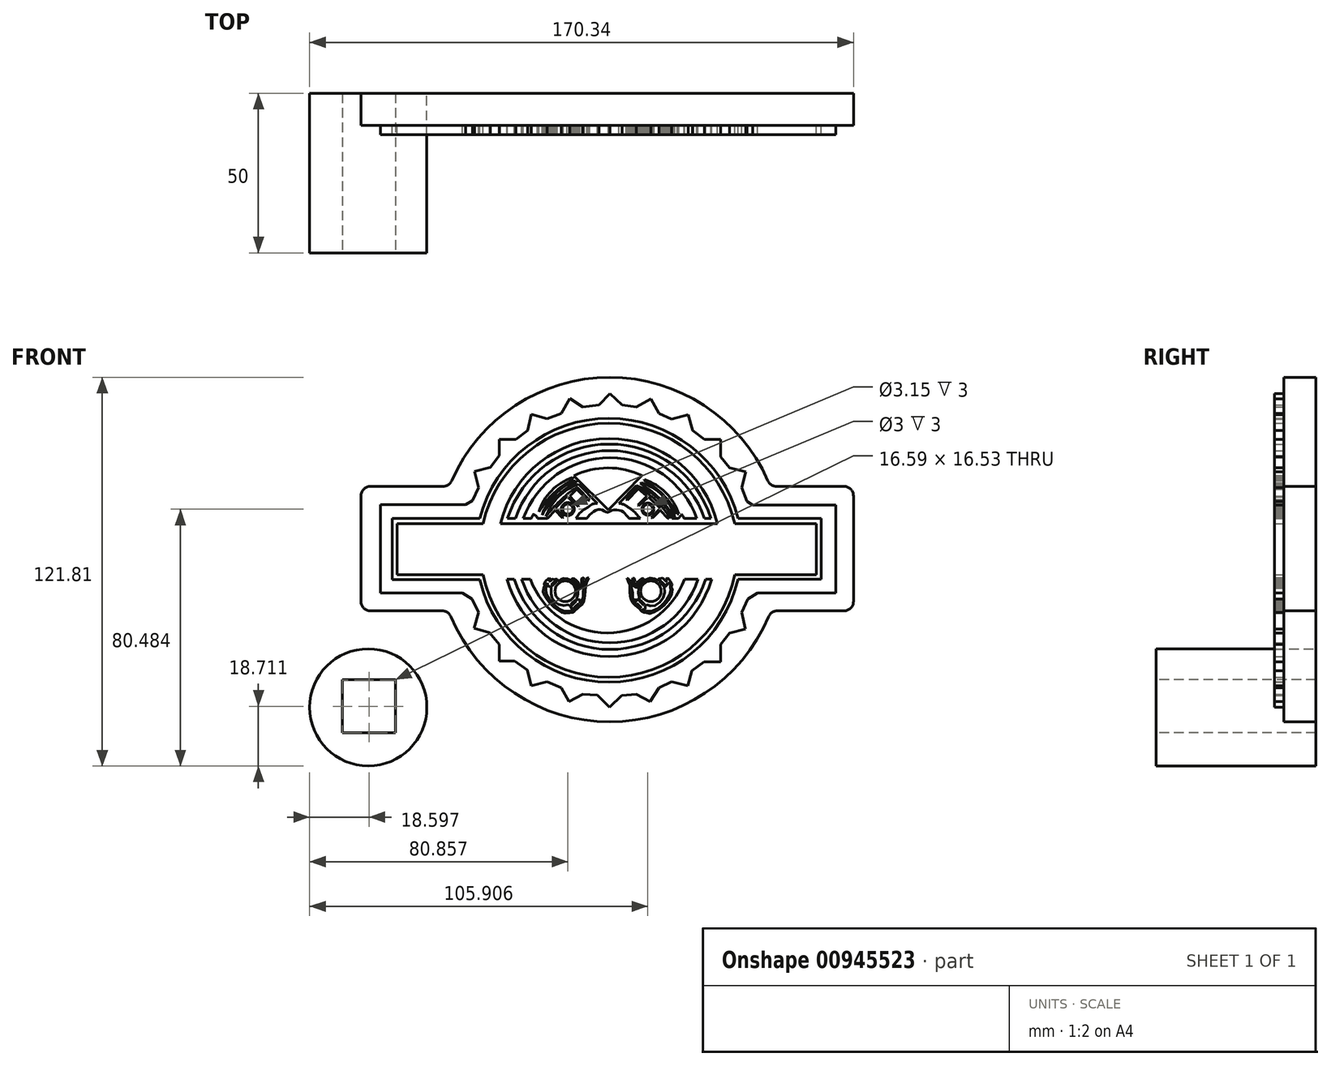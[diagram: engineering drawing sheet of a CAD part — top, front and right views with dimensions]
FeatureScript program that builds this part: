
annotation { "Feature Type Name" : "Feature", "Feature Type Description" : "" }
export const myFeature = defineFeature(function(context is Context, id is Id, definition is map)
    precondition{}
    {
        {
            var Q0;
            Q0=qCreatedBy(makeId("Front.planeOp"),FACE);
            var sketch = newSketch(context, id + "F0", { "sketchPlane" : qUnion([Q0])});
            skArc(sketch, "E0", {"start": v(25.18, 30.24) * mm, "mid": v(75.64, -4.55) * mm, "end": v(126.1, 30.24) * mm});
            skLineSegment(sketch, "E1.0", {"start": v(-2.31, 69.26) * mm, "end": v(25.4, 69.26) * mm});
            skLineSegment(sketch, "E1.1", {"start": v(-2.31, 69.26) * mm, "end": v(-2.31, 30.24) * mm});
            skLineSegment(sketch, "E1.2", {"start": v(-2.31, 30.24) * mm, "end": v(25.18, 30.24) * mm});
            skLineSegment(sketch, "E1.3", {"start": v(151.98, 69.26) * mm, "end": v(151.98, 30.24) * mm});
            skLineSegment(sketch, "E2.trimOffspring", {"start": v(125.88, 69.26) * mm, "end": v(151.98, 69.26) * mm});
            skArc(sketch, "E3.trimOffspring", {"start": v(125.88, 69.26) * mm, "mid": v(75.64, 103.45) * mm, "end": v(25.4, 69.26) * mm});
            skLineSegment(sketch, "E4.trimOffspring", {"start": v(126.1, 30.24) * mm, "end": v(151.98, 30.24) * mm});
            skSolve(sketch);
        }
        {
            var Q0;
            Q0=qCreatedBy(makeId("Front.planeOp"),FACE);
            var sketch = newSketch(context, id + "F1", { "sketchPlane" : qUnion([Q0])});
            skLineSegment(sketch, "E5", {"start": v(30.5, 63.54) * mm, "end": v(3.78, 63.54) * mm});
            skLineSegment(sketch, "E6", {"start": v(3.78, 63.54) * mm, "end": v(3.78, 35.86) * mm});
            skLineSegment(sketch, "E7", {"start": v(3.78, 35.86) * mm, "end": v(29.45, 35.86) * mm});
            skLineSegment(sketch, "E8", {"start": v(29.45, 35.86) * mm, "end": v(32.5, 33.94) * mm});
            skLineSegment(sketch, "E9", {"start": v(32.5, 33.94) * mm, "end": v(34.52, 29.75) * mm});
            skLineSegment(sketch, "E10", {"start": v(34.52, 29.75) * mm, "end": v(33.12, 24.77) * mm});
            skLineSegment(sketch, "E11", {"start": v(33.12, 24.77) * mm, "end": v(37.98, 23.4) * mm});
            skLineSegment(sketch, "E12", {"start": v(37.98, 23.4) * mm, "end": v(40.98, 19.7) * mm});
            skLineSegment(sketch, "E13", {"start": v(40.98, 19.7) * mm, "end": v(40.98, 14.56) * mm});
            skLineSegment(sketch, "E14", {"start": v(40.98, 14.56) * mm, "end": v(45.87, 14.56) * mm});
            skLineSegment(sketch, "E15", {"start": v(45.87, 14.56) * mm, "end": v(49.8, 11.67) * mm});
            skLineSegment(sketch, "E16", {"start": v(49.8, 11.67) * mm, "end": v(51.1, 6.79) * mm});
            skLineSegment(sketch, "E17", {"start": v(51.1, 6.79) * mm, "end": v(55.98, 8.09) * mm});
            skLineSegment(sketch, "E18", {"start": v(55.98, 8.09) * mm, "end": v(60.45, 6.09) * mm});
            skLineSegment(sketch, "E19", {"start": v(60.45, 6.09) * mm, "end": v(62.83, 1.76) * mm});
            skLineSegment(sketch, "E20", {"start": v(62.83, 1.76) * mm, "end": v(67.2, 4.17) * mm});
            skLineSegment(sketch, "E21", {"start": v(67.2, 4.17) * mm, "end": v(71.82, 3.86) * mm});
            skLineSegment(sketch, "E22", {"start": v(71.82, 3.86) * mm, "end": v(75.57, 0) * mm});
            skLineSegment(sketch, "E23", {"start": v(75.57, 0) * mm, "end": v(79.4, 3.73) * mm});
            skLineSegment(sketch, "E24", {"start": v(79.4, 3.73) * mm, "end": v(84.01, 4.17) * mm});
            skLineSegment(sketch, "E25", {"start": v(84.01, 4.17) * mm, "end": v(88.3, 1.76) * mm});
            skLineSegment(sketch, "E26", {"start": v(88.3, 1.76) * mm, "end": v(91.06, 6.09) * mm});
            skLineSegment(sketch, "E27", {"start": v(91.06, 6.09) * mm, "end": v(95.06, 8.09) * mm});
            skLineSegment(sketch, "E28", {"start": v(95.06, 8.09) * mm, "end": v(100.1, 6.76) * mm});
            skLineSegment(sketch, "E29", {"start": v(100.1, 6.76) * mm, "end": v(101.35, 11.5) * mm});
            skLineSegment(sketch, "E30", {"start": v(101.35, 11.5) * mm, "end": v(105.12, 14.32) * mm});
            skLineSegment(sketch, "E31", {"start": v(105.12, 14.32) * mm, "end": v(110.37, 14.32) * mm});
            skLineSegment(sketch, "E32", {"start": v(110.37, 14.32) * mm, "end": v(110.37, 19.7) * mm});
            skLineSegment(sketch, "E33", {"start": v(110.37, 19.7) * mm, "end": v(113.14, 23.25) * mm});
            skLineSegment(sketch, "E34", {"start": v(113.14, 23.25) * mm, "end": v(118.13, 24.58) * mm});
            skLineSegment(sketch, "E35", {"start": v(118.13, 24.58) * mm, "end": v(116.98, 29.75) * mm});
            skLineSegment(sketch, "E36", {"start": v(116.98, 29.75) * mm, "end": v(118.86, 33.93) * mm});
            skLineSegment(sketch, "E37", {"start": v(118.86, 33.93) * mm, "end": v(121.91, 35.86) * mm});
            skLineSegment(sketch, "E38", {"start": v(121.91, 35.86) * mm, "end": v(146.4, 35.86) * mm});
            skLineSegment(sketch, "E39", {"start": v(146.4, 35.86) * mm, "end": v(146.4, 63.36) * mm});
            skLineSegment(sketch, "E40", {"start": v(146.4, 63.36) * mm, "end": v(120.45, 63.36) * mm});
            skLineSegment(sketch, "E41", {"start": v(120.45, 63.36) * mm, "end": v(118.6, 64.53) * mm});
            skLineSegment(sketch, "E42", {"start": v(118.6, 64.53) * mm, "end": v(117.02, 68.85) * mm});
            skLineSegment(sketch, "E43", {"start": v(117.02, 68.85) * mm, "end": v(118.21, 73.83) * mm});
            skLineSegment(sketch, "E44", {"start": v(118.21, 73.83) * mm, "end": v(113.14, 75.04) * mm});
            skLineSegment(sketch, "E45", {"start": v(113.14, 75.04) * mm, "end": v(110.4, 78.55) * mm});
            skLineSegment(sketch, "E46", {"start": v(110.4, 78.55) * mm, "end": v(110.4, 83.96) * mm});
            skLineSegment(sketch, "E47", {"start": v(110.4, 83.96) * mm, "end": v(105.25, 83.96) * mm});
            skLineSegment(sketch, "E48", {"start": v(105.25, 83.96) * mm, "end": v(101.62, 86.75) * mm});
            skLineSegment(sketch, "E49", {"start": v(101.62, 86.75) * mm, "end": v(100.26, 91.8) * mm});
            skLineSegment(sketch, "E50", {"start": v(100.26, 91.8) * mm, "end": v(95, 90.39) * mm});
            skLineSegment(sketch, "E51", {"start": v(95, 90.39) * mm, "end": v(91.04, 92.16) * mm});
            skLineSegment(sketch, "E52", {"start": v(91.04, 92.16) * mm, "end": v(88.5, 96.65) * mm});
            skLineSegment(sketch, "E53", {"start": v(88.5, 96.65) * mm, "end": v(84.01, 94.11) * mm});
            skLineSegment(sketch, "E54", {"start": v(84.01, 94.11) * mm, "end": v(79.45, 94.74) * mm});
            skLineSegment(sketch, "E55", {"start": v(79.45, 94.74) * mm, "end": v(75.74, 98.35) * mm});
            skLineSegment(sketch, "E56", {"start": v(75.74, 98.35) * mm, "end": v(72.22, 94.74) * mm});
            skLineSegment(sketch, "E57", {"start": v(72.22, 94.74) * mm, "end": v(67.2, 94.19) * mm});
            skLineSegment(sketch, "E58", {"start": v(67.2, 94.19) * mm, "end": v(63.1, 96.84) * mm});
            skLineSegment(sketch, "E59", {"start": v(63.1, 96.84) * mm, "end": v(60.45, 92.16) * mm});
            skLineSegment(sketch, "E60", {"start": v(60.45, 92.16) * mm, "end": v(55.98, 90.42) * mm});
            skLineSegment(sketch, "E61", {"start": v(55.98, 90.42) * mm, "end": v(51.1, 91.9) * mm});
            skLineSegment(sketch, "E62", {"start": v(51.1, 91.9) * mm, "end": v(49.88, 86.75) * mm});
            skLineSegment(sketch, "E63", {"start": v(49.88, 86.75) * mm, "end": v(46.18, 83.96) * mm});
            skLineSegment(sketch, "E64", {"start": v(46.18, 83.96) * mm, "end": v(40.98, 83.96) * mm});
            skLineSegment(sketch, "E65", {"start": v(40.98, 83.96) * mm, "end": v(40.98, 78.87) * mm});
            skLineSegment(sketch, "E66", {"start": v(40.98, 78.87) * mm, "end": v(38.2, 75.25) * mm});
            skLineSegment(sketch, "E67", {"start": v(38.2, 75.25) * mm, "end": v(33.23, 73.92) * mm});
            skLineSegment(sketch, "E68", {"start": v(33.23, 73.92) * mm, "end": v(34.52, 68.85) * mm});
            skLineSegment(sketch, "E69", {"start": v(34.52, 68.85) * mm, "end": v(32.7, 64.8) * mm});
            skLineSegment(sketch, "E70", {"start": v(32.7, 64.8) * mm, "end": v(30.5, 63.54) * mm});
            skLineSegment(sketch, "E71", {"start": v(9.03, 41.6) * mm, "end": v(35.92, 41.6) * mm});
            skLineSegment(sketch, "E72", {"start": v(41.42, 41.6) * mm, "end": v(109.35, 41.6) * mm});
            skLineSegment(sketch, "E73", {"start": v(114.78, 41.6) * mm, "end": v(140.34, 41.6) * mm});
            skLineSegment(sketch, "E74", {"start": v(140.34, 41.6) * mm, "end": v(140.34, 57.63) * mm});
            skLineSegment(sketch, "E75", {"start": v(140.34, 57.63) * mm, "end": v(114.78, 57.63) * mm});
            skLineSegment(sketch, "E76", {"start": v(109.35, 57.63) * mm, "end": v(41.42, 57.63) * mm});
            skLineSegment(sketch, "E77", {"start": v(35.92, 57.63) * mm, "end": v(9.03, 57.63) * mm});
            skLineSegment(sketch, "E78", {"start": v(9.03, 57.63) * mm, "end": v(9.03, 41.6) * mm});
            skLineSegment(sketch, "E79", {"start": v(34.93, 40.01) * mm, "end": v(7.52, 40.01) * mm});
            skLineSegment(sketch, "E80", {"start": v(7.52, 40.01) * mm, "end": v(7.52, 59.18) * mm});
            skLineSegment(sketch, "E81", {"start": v(7.52, 59.18) * mm, "end": v(34.93, 59.18) * mm});
            skLineSegment(sketch, "E82", {"start": v(33.62, 37.96) * mm, "end": v(5.73, 37.96) * mm});
            skLineSegment(sketch, "E83", {"start": v(5.73, 37.96) * mm, "end": v(5.73, 61.27) * mm});
            skLineSegment(sketch, "E84", {"start": v(5.73, 61.27) * mm, "end": v(33.62, 61.27) * mm});
            skLineSegment(sketch, "E85", {"start": v(117.62, 37.9) * mm, "end": v(144.3, 37.9) * mm});
            skLineSegment(sketch, "E86", {"start": v(144.3, 37.9) * mm, "end": v(144.3, 61.3) * mm});
            skLineSegment(sketch, "E87", {"start": v(144.3, 61.3) * mm, "end": v(117.62, 61.3) * mm});
            skLineSegment(sketch, "E88", {"start": v(115.83, 40.18) * mm, "end": v(141.89, 40.18) * mm});
            skLineSegment(sketch, "E89", {"start": v(141.89, 40.18) * mm, "end": v(141.89, 59.2) * mm});
            skLineSegment(sketch, "E90", {"start": v(141.89, 59.2) * mm, "end": v(115.83, 59.2) * mm});
            skArc(sketch, "E91", {"start": v(117.62, 61.3) * mm, "mid": v(75.61, 92.75) * mm, "end": v(33.62, 61.27) * mm});
            skArc(sketch, "E92", {"start": v(33.62, 37.96) * mm, "mid": v(75.6, 5.72) * mm, "end": v(117.62, 37.9) * mm});
            skArc(sketch, "E93", {"start": v(115.83, 59.2) * mm, "mid": v(75.38, 90.6) * mm, "end": v(34.93, 59.18) * mm});
            skArc(sketch, "E94", {"start": v(114.78, 57.63) * mm, "mid": v(75.35, 89.03) * mm, "end": v(35.92, 57.63) * mm});
            skArc(sketch, "E95", {"start": v(34.93, 40.01) * mm, "mid": v(75.45, 7.9) * mm, "end": v(115.83, 40.18) * mm});
            skArc(sketch, "E96", {"start": v(35.92, 41.6) * mm, "mid": v(75.35, 9.41) * mm, "end": v(114.78, 41.6) * mm});
            skArc(sketch, "E97", {"start": v(109.35, 57.63) * mm, "mid": v(75.39, 84.29) * mm, "end": v(41.42, 57.63) * mm});
            skArc(sketch, "E98", {"start": v(41.42, 41.6) * mm, "mid": v(75.39, 14.36) * mm, "end": v(109.35, 41.6) * mm});
            skLineSegment(sketch, "E99", {"start": v(43.44, 40.2) * mm, "end": v(45.7, 40.2) * mm});
            skLineSegment(sketch, "E100", {"start": v(107.38, 59.2) * mm, "end": v(105.28, 59.2) * mm});
            skArc(sketch, "E101", {"start": v(43.44, 40.2) * mm, "mid": v(75.49, 15.92) * mm, "end": v(107.53, 40.2) * mm});
            skArc(sketch, "E102", {"start": v(45.7, 40.2) * mm, "mid": v(75.66, 18.15) * mm, "end": v(105.62, 40.2) * mm});
            skArc(sketch, "E103", {"start": v(48.04, 40.2) * mm, "mid": v(75.68, 20.21) * mm, "end": v(103.32, 40.2) * mm});
            skArc(sketch, "E104", {"start": v(50.75, 40.2) * mm, "mid": v(74.89, 23.3) * mm, "end": v(99.03, 40.2) * mm});
            skArc(sketch, "E105", {"start": v(107.38, 59.2) * mm, "mid": v(75.5, 82.51) * mm, "end": v(43.63, 59.2) * mm});
            skArc(sketch, "E106", {"start": v(105.28, 59.2) * mm, "mid": v(75.68, 80.48) * mm, "end": v(46.08, 59.2) * mm});
            skArc(sketch, "E107", {"start": v(102.92, 59.2) * mm, "mid": v(75.72, 78.24) * mm, "end": v(48.53, 59.2) * mm});
            skLineSegment(sketch, "E108.trimOffspring", {"start": v(46.08, 59.2) * mm, "end": v(43.63, 59.2) * mm});
            skLineSegment(sketch, "E109.trimOffspring", {"start": v(102.92, 59.2) * mm, "end": v(98.91, 59.2) * mm});
            skLineSegment(sketch, "E110.trimOffspring", {"start": v(105.62, 40.2) * mm, "end": v(107.53, 40.2) * mm});
            skLineSegment(sketch, "E111.trimOffspring", {"start": v(48.04, 40.2) * mm, "end": v(50.75, 40.2) * mm});
            skLineSegment(sketch, "E112.trimOffspring", {"start": v(99.03, 40.2) * mm, "end": v(103.32, 40.2) * mm});
            skCircle(sketch, "E113", {"center": v(61.71, 36.41) * mm, "radius": 3.23 * mm});
            skCircle(sketch, "E114", {"center": v(88.52, 36.41) * mm, "radius": 3.23 * mm});
            skFitSpline(sketch, "E115", {"points": [v(68.46, 59.2) * mm, v(69.7, 60.65) * mm, v(71.48, 61.83) * mm, v(73.15, 61.95) * mm, v(74.42, 61.27) * mm, v(75.13, 61.15) * mm, v(75.93, 61.58) * mm, v(77.56, 61.95) * mm, v(79.42, 61.49) * mm, v(80.68, 60.44) * mm, v(81.6, 59.2) * mm], "startDerivative": vector(10.07, 13.37) * mm, "endDerivative": vector(8.68, -12.6) * mm});
            skLineSegment(sketch, "E116.trimOffspring", {"start": v(68.46, 59.2) * mm, "end": v(64.99, 59.2) * mm});
            skLineSegment(sketch, "E117", {"start": v(85.75, 72.69) * mm, "end": v(75.16, 61.95) * mm});
            skLineSegment(sketch, "E118", {"start": v(75.16, 61.95) * mm, "end": v(64.39, 72.57) * mm});
            skArc(sketch, "E119", {"start": v(85.75, 72.69) * mm, "mid": v(75.05, 75.05) * mm, "end": v(64.39, 72.57) * mm});
            skFitSpline(sketch, "E120", {"points": [v(51.11, 59.2) * mm, v(51.37, 59.89) * mm, v(51.77, 60.51) * mm, v(51.88, 60.44) * mm, v(52.58, 60) * mm, v(52.99, 59.2) * mm], "startDerivative": vector(0.9, 2.92) * mm, "endDerivative": vector(1.1, -3.69) * mm});
            skFitSpline(sketch, "E121", {"points": [v(98.91, 59.2) * mm, v(98.65, 59.79) * mm, v(98.16, 60.47) * mm, v(98.07, 60.32) * mm, v(97.9, 60.15) * mm, v(97.17, 59.2) * mm], "startDerivative": vector(-0.86, 2.35) * mm, "endDerivative": vector(-2.85, -4.03) * mm});
            skLineSegment(sketch, "E122.trimOffspring", {"start": v(97.17, 59.2) * mm, "end": v(95.18, 59.2) * mm});
            skLineSegment(sketch, "E123.trimOffspring", {"start": v(51.11, 59.2) * mm, "end": v(48.53, 59.2) * mm});
            skFitSpline(sketch, "E124", {"points": [v(56.7, 40.5) * mm, v(55.45, 39.36) * mm, v(55.2, 38.92) * mm, v(55.12, 38.3) * mm, v(55.2, 37.75) * mm, v(54.9, 37.42) * mm, v(54.79, 36.98) * mm, v(54.83, 36.02) * mm, v(55.56, 34.63) * mm, v(56.26, 33.38) * mm, v(57.73, 31.8) * mm, v(59.34, 30.52) * mm, v(60.66, 29.75) * mm, v(61.65, 29.56) * mm, v(63.09, 29.67) * mm, v(63.6, 29.78) * mm, v(64.15, 29.75) * mm, v(64.52, 30.08) * mm, v(66.13, 31.5) * mm, v(67.09, 32.54) * mm, v(67.75, 34.04) * mm, v(67.93, 36.13) * mm, v(68.04, 37.57) * mm, v(68.45, 39.4) * mm, v(69.03, 40.5) * mm], "startDerivative": vector(-29.77, -25.32) * mm, "endDerivative": vector(14.74, 22.92) * mm});
            skFitSpline(sketch, "E125", {"points": [v(81, 40.5) * mm, v(81.44, 39.49) * mm, v(81.91, 38.35) * mm, v(81.91, 37.5) * mm, v(81.95, 35.96) * mm, v(82.06, 34.68) * mm, v(82.43, 33.5) * mm, v(83.16, 32.44) * mm, v(84.3, 31.4) * mm, v(85.51, 30.3) * mm, v(85.92, 29.83) * mm, v(86.94, 29.8) * mm, v(87.5, 29.5) * mm, v(88.27, 29.43) * mm, v(90.8, 30.57) * mm, v(93.3, 32.73) * mm, v(95.13, 35.7) * mm, v(95.06, 37.5) * mm, v(94.87, 37.76) * mm, v(95.17, 38.42) * mm, v(94.73, 39.34) * mm, v(93.8, 40.5) * mm], "startDerivative": vector(9.2, -22.5) * mm, "endDerivative": vector(-18.31, 23.3) * mm});
            skFitSpline(sketch, "E126", {"points": [v(93.8, 40.5) * mm, v(93.16, 40.5) * mm, v(93.2, 40.38) * mm, v(93.4, 40.1) * mm, v(93.5, 39.91) * mm, v(93.5, 39.65) * mm, v(93.4, 39.44) * mm, v(93.3, 39.34) * mm, v(93.18, 39.44) * mm, v(92.9, 39.78) * mm, v(92.55, 40.22) * mm, v(92.31, 40.5) * mm, v(92.14, 40.5) * mm, v(90.9, 40.5) * mm, v(91.02, 40.33) * mm, v(91.05, 40.12) * mm, v(90.96, 39.87) * mm, v(90.66, 39.76) * mm, v(90.5, 39.73) * mm, v(90.04, 40.04) * mm, v(89.5, 40.35) * mm, v(88.64, 40.5) * mm, v(87.72, 40.4) * mm, v(86.86, 39.96) * mm, v(86.02, 39.34) * mm, v(85.32, 38.55) * mm, v(84.81, 37.72) * mm, v(84.56, 36.62) * mm, v(84.64, 35.27) * mm, v(84.98, 34.38) * mm, v(85.02, 34.15) * mm, v(84.91, 33.68) * mm, v(84.7, 33.68) * mm, v(83.94, 33.73) * mm, v(83.79, 33.72) * mm, v(83.8, 33.58) * mm, v(83.82, 32.72) * mm, v(83.8, 32.62) * mm, v(83.63, 32.6) * mm, v(83.49, 32.75) * mm, v(83.12, 33.23) * mm, v(83.12, 33.57) * mm, v(83.14, 34.03) * mm, v(83.05, 34.2) * mm, v(82.75, 34.4) * mm, v(82.75, 34.62) * mm, v(82.83, 36.84) * mm, v(82.67, 37.1) * mm, v(82.32, 37.49) * mm, v(82.4, 37.86) * mm, v(82.44, 38.04) * mm, v(82.44, 38.42) * mm, v(82.09, 39.34) * mm, v(81.67, 40.4) * mm, v(81, 40.5) * mm], "startDerivative": vector(-41.62, 3.97) * mm, "endDerivative": vector(-33.99, -3.31) * mm});
            skFitSpline(sketch, "E127", {"points": [v(82.8, 40.5) * mm, v(83.16, 40.5) * mm, v(83.38, 40.32) * mm, v(83.5, 39.88) * mm, v(83.53, 39.34) * mm, v(83.5, 38.84) * mm, v(83.52, 38.42) * mm, v(83.58, 38.22) * mm, v(83.83, 38.06) * mm, v(83.95, 38.08) * mm, v(84.06, 38.42) * mm, v(84.36, 39.08) * mm, v(84.8, 39.65) * mm, v(85.2, 40.02) * mm, v(85.69, 40.35) * mm, v(86.02, 40.5) * mm, v(86.17, 40.32) * mm, v(86.22, 40.1) * mm, v(86.11, 39.98) * mm, v(85.75, 39.73) * mm, v(85.32, 39.34) * mm, v(84.88, 38.71) * mm, v(84.62, 38.26) * mm, v(84.44, 37.8) * mm, v(84.25, 37.57) * mm, v(83.8, 37.6) * mm, v(83.5, 37.69) * mm, v(83.18, 37.97) * mm, v(83.05, 38.23) * mm, v(82.88, 38.55) * mm, v(82.77, 38.8) * mm, v(82.74, 40.28) * mm, v(82.8, 40.5) * mm]});
            skFitSpline(sketch, "E128", {"points": [v(93.8, 38.99) * mm, v(94.46, 39.05) * mm, v(94.55, 39.01) * mm, v(94.56, 38.76) * mm, v(94.58, 37.7) * mm, v(94.6, 37.5) * mm, v(94.73, 36.96) * mm, v(94.73, 36.2) * mm, v(94.3, 34.96) * mm, v(93.36, 33.56) * mm, v(92.17, 32.2) * mm, v(90.82, 31.12) * mm, v(89.2, 30.26) * mm, v(88.08, 30.01) * mm, v(87.78, 30.13) * mm, v(86.72, 30.31) * mm, v(86.17, 30.31) * mm, v(86.13, 30.4) * mm, v(85.86, 30.7) * mm, v(86.02, 30.73) * mm, v(86.7, 30.78) * mm, v(86.73, 31) * mm, v(86.72, 31.8) * mm, v(86.85, 31.83) * mm, v(87.13, 32.1) * mm, v(87.17, 32.17) * mm, v(87.4, 32.1) * mm, v(87.8, 31.9) * mm, v(88.89, 31.75) * mm, v(89.95, 31.93) * mm, v(91.2, 32.8) * mm, v(92.25, 34.06) * mm, v(92.84, 35.5) * mm, v(92.8, 37.18) * mm, v(92.68, 37.94) * mm, v(92.73, 37.96) * mm, v(92.82, 37.96) * mm, v(93.4, 38.02) * mm, v(93.48, 38.18) * mm, v(93.43, 38.42) * mm, v(93.6, 38.42) * mm, v(93.8, 38.42) * mm, v(93.8, 38.99) * mm]});
            skFitSpline(sketch, "E129", {"points": [v(56.7, 40.5) * mm, v(56.93, 40.39) * mm, v(57, 40.18) * mm, v(56.81, 39.99) * mm, v(56.7, 39.8) * mm, v(56.6, 39.64) * mm, v(56.7, 39.51) * mm, v(56.92, 39.52) * mm, v(57.2, 39.75) * mm, v(57.34, 39.98) * mm, v(57.65, 40.24) * mm, v(57.86, 40.33) * mm, v(58, 40.14) * mm, v(58.47, 40.04) * mm, v(58.82, 40.23) * mm, v(59.1, 40.29) * mm, v(59.18, 40) * mm, v(59.16, 39.76) * mm, v(59.43, 39.7) * mm, v(59.89, 39.75) * mm, v(60.05, 39.98) * mm, v(60.4, 40.19) * mm, v(61.02, 40.37) * mm, v(62.12, 40.36) * mm, v(63.06, 40.08) * mm, v(64.05, 39.36) * mm, v(64.89, 38.5) * mm, v(65.33, 37.63) * mm, v(65.63, 36.52) * mm, v(65.62, 35.57) * mm, v(65.42, 34.6) * mm, v(65.2, 34.12) * mm, v(65.21, 34) * mm, v(65.25, 33.8) * mm, v(65.25, 33.7) * mm, v(65.31, 33.72) * mm, v(66.26, 33.78) * mm, v(66.28, 33.78) * mm], "startDerivative": vector(11.53, -3.8) * mm, "endDerivative": vector(1.43, -0.09) * mm});
            skFitSpline(sketch, "E130", {"points": [v(66.28, 33.78) * mm, v(66.28, 32.68) * mm, v(66.28, 32.65) * mm, v(66.49, 32.66) * mm, v(66.64, 32.82) * mm, v(66.93, 33.27) * mm, v(66.93, 34) * mm, v(67.02, 34) * mm, v(67.18, 34) * mm, v(67.36, 35.18) * mm, v(67.35, 36.04) * mm, v(67.53, 37.27) * mm, v(67.71, 38.22) * mm, v(68, 39.36) * mm, v(68.41, 40.37) * mm, v(68.47, 40.5) * mm, v(69.03, 40.5) * mm], "startDerivative": vector(0.42, -16.56) * mm, "endDerivative": vector(11.55, -1.06) * mm});
            skFitSpline(sketch, "E131", {"points": [v(56.17, 39.01) * mm, v(56.19, 38.04) * mm, v(56.22, 38) * mm, v(57.2, 37.98) * mm, v(57.23, 37.91) * mm, v(57.27, 37.32) * mm, v(57.26, 36.74) * mm, v(57.23, 35.98) * mm, v(57.28, 35.1) * mm, v(57.67, 34) * mm, v(58.46, 33.09) * mm, v(59.42, 32.4) * mm, v(60.9, 31.94) * mm, v(62.35, 32) * mm, v(62.84, 32.22) * mm, v(62.9, 32.22) * mm, v(62.99, 32.12) * mm, v(63.03, 31.87) * mm, v(63.14, 31.85) * mm, v(63.34, 31.87) * mm, v(63.35, 31.81) * mm, v(63.43, 31.26) * mm, v(63.67, 31.12) * mm, v(63.8, 30.9) * mm, v(64.33, 30.85) * mm, v(64.46, 30.81) * mm, v(64.5, 30.69) * mm, v(64.34, 30.61) * mm, v(64.02, 30.56) * mm, v(63.81, 30.36) * mm, v(62.99, 30.16) * mm, v(61, 30.2) * mm, v(59.42, 31.16) * mm, v(57.73, 32.68) * mm, v(56, 35.08) * mm, v(55.66, 36.3) * mm, v(55.68, 37.42) * mm, v(55.82, 38.58) * mm, v(55.97, 39.06) * mm, v(56.17, 39.01) * mm]});
            skFitSpline(sketch, "E132", {"points": [v(67.09, 40.5) * mm, v(67.44, 40.5) * mm, v(67.48, 40.5) * mm, v(67.54, 39.86) * mm, v(67.37, 39.07) * mm, v(67.3, 38.44) * mm, v(66.97, 37.94) * mm, v(66.66, 37.42) * mm, v(66.28, 37.29) * mm, v(66, 37.6) * mm, v(65.47, 38.7) * mm, v(64.65, 39.56) * mm, v(63.74, 40.34) * mm, v(63.93, 40.4) * mm, v(64.4, 40.36) * mm, v(64.73, 40.17) * mm, v(65.62, 39.36) * mm, v(66.09, 38.53) * mm, v(66.28, 38.08) * mm, v(66.48, 38.1) * mm, v(66.75, 38.82) * mm, v(66.87, 39.83) * mm, v(66.88, 40.5) * mm, v(67.09, 40.5) * mm]});
            skArc(sketch, "E133", {"start": v(58.37, 39) * mm, "mid": v(58.7, 39.44) * mm, "end": v(58.22, 39.17) * mm});
            skArc(sketch, "E134", {"start": v(58.03, 38.64) * mm, "mid": v(58.3, 38.72) * mm, "end": v(58.37, 39) * mm});
            skArc(sketch, "E135", {"start": v(57.83, 38.83) * mm, "mid": v(57.57, 38.35) * mm, "end": v(58.03, 38.64) * mm});
            skArc(sketch, "E136.trimOffspring", {"start": v(58.22, 39.17) * mm, "mid": v(57.91, 39.13) * mm, "end": v(57.83, 38.83) * mm});
            skArc(sketch, "E137", {"start": v(64.59, 32.8) * mm, "mid": v(64.86, 33.32) * mm, "end": v(64.33, 33.09) * mm});
            skArc(sketch, "E138", {"start": v(64.33, 33.09) * mm, "mid": v(64.07, 32.99) * mm, "end": v(64.02, 32.72) * mm});
            skArc(sketch, "E139", {"start": v(64.02, 32.72) * mm, "mid": v(63.7, 32.21) * mm, "end": v(64.22, 32.52) * mm});
            skArc(sketch, "E140", {"start": v(65.63, 31.78) * mm, "mid": v(65.89, 32.28) * mm, "end": v(65.4, 32) * mm});
            skArc(sketch, "E141", {"start": v(65.4, 32) * mm, "mid": v(65.14, 31.92) * mm, "end": v(65.06, 31.66) * mm});
            skArc(sketch, "E142", {"start": v(65.06, 31.66) * mm, "mid": v(64.78, 31.17) * mm, "end": v(65.28, 31.42) * mm});
            skArc(sketch, "E143.trimOffspring", {"start": v(64.22, 32.52) * mm, "mid": v(64.47, 32.57) * mm, "end": v(64.59, 32.8) * mm});
            skArc(sketch, "E144.trimOffspring", {"start": v(65.28, 31.42) * mm, "mid": v(65.56, 31.5) * mm, "end": v(65.63, 31.78) * mm});
            skPoint(sketch, "E145.0.internal.orphan", {"position": v(91.27, 39.34) * mm});
            skPoint(sketch, "E145.2.internal.orphan", {"position": v(91.77, 38.55) * mm});
            skPoint(sketch, "E145.6.internal.orphan", {"position": v(92.67, 38.42) * mm});
            skArc(sketch, "E146", {"start": v(85.67, 33.03) * mm, "mid": v(85.22, 33.34) * mm, "end": v(85.51, 32.88) * mm});
            skArc(sketch, "E147", {"start": v(85.99, 32.7) * mm, "mid": v(85.93, 32.96) * mm, "end": v(85.67, 33.03) * mm});
            skArc(sketch, "E148", {"start": v(85.86, 32.56) * mm, "mid": v(86.32, 32.24) * mm, "end": v(85.99, 32.7) * mm});
            skArc(sketch, "E149", {"start": v(84.67, 32) * mm, "mid": v(84.21, 32.3) * mm, "end": v(84.45, 31.81) * mm});
            skArc(sketch, "E150", {"start": v(84.45, 31.81) * mm, "mid": v(84.54, 31.56) * mm, "end": v(84.81, 31.54) * mm});
            skArc(sketch, "E151", {"start": v(84.81, 31.54) * mm, "mid": v(85.27, 31.26) * mm, "end": v(84.93, 31.68) * mm});
            skArc(sketch, "E152", {"start": v(91.8, 39.19) * mm, "mid": v(91.38, 39.53) * mm, "end": v(91.7, 39.1) * mm});
            skArc(sketch, "E153", {"start": v(91.7, 39.1) * mm, "mid": v(91.74, 38.74) * mm, "end": v(92.09, 38.7) * mm});
            skArc(sketch, "E154", {"start": v(92.09, 38.7) * mm, "mid": v(92.58, 38.32) * mm, "end": v(92.2, 38.8) * mm});
            skArc(sketch, "E155.trimOffspring", {"start": v(92.2, 38.8) * mm, "mid": v(92.14, 39.15) * mm, "end": v(91.8, 39.19) * mm});
            skArc(sketch, "E156.trimOffspring", {"start": v(84.93, 31.68) * mm, "mid": v(84.9, 31.91) * mm, "end": v(84.67, 32) * mm});
            skArc(sketch, "E157.trimOffspring", {"start": v(85.51, 32.88) * mm, "mid": v(85.58, 32.6) * mm, "end": v(85.86, 32.56) * mm});
            skArc(sketch, "E158", {"start": v(63.95, 72) * mm, "mid": v(57.38, 67.9) * mm, "end": v(53.42, 61.23) * mm});
            skArc(sketch, "E159", {"start": v(64.94, 70.98) * mm, "mid": v(58.5, 66.8) * mm, "end": v(54.44, 60.3) * mm});
            skArc(sketch, "E160", {"start": v(65.9, 69.9) * mm, "mid": v(59.62, 66.05) * mm, "end": v(55.67, 59.84) * mm});
            skArc(sketch, "E161", {"start": v(64.23, 71.5) * mm, "mid": v(58.1, 67.13) * mm, "end": v(53.42, 61.23) * mm});
            skArc(sketch, "E162", {"start": v(65.28, 70.46) * mm, "mid": v(59.08, 66.2) * mm, "end": v(54.44, 60.3) * mm});
            skArc(sketch, "E163", {"start": v(65.18, 68.88) * mm, "mid": v(60.07, 64.74) * mm, "end": v(55.67, 59.84) * mm});
            skCircle(sketch, "E164", {"center": v(62.5, 62.12) * mm, "radius": 1.57 * mm});
            skCircle(sketch, "E165", {"center": v(62.5, 62.12) * mm, "radius": 2.04 * mm});
            skCircle(sketch, "E166", {"center": v(62.5, 62.12) * mm, "radius": 2.53 * mm});
            skCircle(sketch, "E167", {"center": v(87.55, 62.12) * mm, "radius": 1.5 * mm});
            skCircle(sketch, "E168", {"center": v(87.58, 62.13) * mm, "radius": 1.9 * mm});
            skCircle(sketch, "E169", {"center": v(87.58, 62.13) * mm, "radius": 2.44 * mm});
            skArc(sketch, "E170", {"start": v(97.24, 60.63) * mm, "mid": v(93.17, 67.27) * mm, "end": v(86.55, 71.38) * mm});
            skArc(sketch, "E171", {"start": v(96.03, 59.53) * mm, "mid": v(92.16, 66.37) * mm, "end": v(85.42, 70.43) * mm});
            skArc(sketch, "E172", {"start": v(95.18, 59.2) * mm, "mid": v(90.7, 65.57) * mm, "end": v(83.98, 69.51) * mm});
            skArc(sketch, "E173", {"start": v(96.8, 60.63) * mm, "mid": v(92.35, 66.65) * mm, "end": v(86.37, 71.18) * mm});
            skArc(sketch, "E174", {"start": v(95.72, 59.69) * mm, "mid": v(91.14, 65.62) * mm, "end": v(85.18, 70.17) * mm});
            skLineSegment(sketch, "E175", {"start": v(96.8, 60.63) * mm, "end": v(97.24, 60.63) * mm});
            skLineSegment(sketch, "E176", {"start": v(95.72, 59.69) * mm, "end": v(96.03, 59.53) * mm});
            skLineSegment(sketch, "E177", {"start": v(86.55, 71.38) * mm, "end": v(86.37, 71.18) * mm});
            skLineSegment(sketch, "E178", {"start": v(85.42, 70.43) * mm, "end": v(85.18, 70.17) * mm});
            skLineSegment(sketch, "E179", {"start": v(83.98, 69.51) * mm, "end": v(78.5, 63.96) * mm});
            skLineSegment(sketch, "E180", {"start": v(84.4, 68.83) * mm, "end": v(80.82, 65.2) * mm});
            skLineSegment(sketch, "E181", {"start": v(80.82, 65.2) * mm, "end": v(81.16, 64.95) * mm});
            skLineSegment(sketch, "E182", {"start": v(81.16, 64.95) * mm, "end": v(84.62, 68.46) * mm});
            skLineSegment(sketch, "E183", {"start": v(84.62, 68.46) * mm, "end": v(87.25, 66.23) * mm});
            skLineSegment(sketch, "E184", {"start": v(87.25, 66.23) * mm, "end": v(84.49, 63.43) * mm});
            skLineSegment(sketch, "E185", {"start": v(84.49, 63.43) * mm, "end": v(84.74, 63.18) * mm});
            skLineSegment(sketch, "E186", {"start": v(84.74, 63.18) * mm, "end": v(87.75, 66.01) * mm});
            skLineSegment(sketch, "E187", {"start": v(87.75, 66.01) * mm, "end": v(91.41, 62.4) * mm});
            skLineSegment(sketch, "E188", {"start": v(91.41, 62.4) * mm, "end": v(88.71, 59.44) * mm});
            skLineSegment(sketch, "E189", {"start": v(88.71, 59.44) * mm, "end": v(89.06, 59.38) * mm});
            skLineSegment(sketch, "E190", {"start": v(89.06, 59.38) * mm, "end": v(91.45, 61.8) * mm});
            skLineSegment(sketch, "E191", {"start": v(91.45, 61.8) * mm, "end": v(93.82, 59.2) * mm});
            skLineSegment(sketch, "E192", {"start": v(94.16, 59.2) * mm, "end": v(94.32, 59.68) * mm});
            skArc(sketch, "E193", {"start": v(94.32, 59.68) * mm, "mid": v(90.02, 64.97) * mm, "end": v(84.4, 68.83) * mm});
            skLineSegment(sketch, "E194.trimOffspring", {"start": v(85.18, 59.2) * mm, "end": v(81.6, 59.2) * mm});
            skFitSpline(sketch, "E195", {"points": [v(78.5, 63.96) * mm, v(79.55, 63.75) * mm, v(80.67, 63.26) * mm, v(81.97, 62.35) * mm, v(83.16, 61.47) * mm, v(85.18, 59.2) * mm], "startDerivative": vector(6.53, -1.02) * mm, "endDerivative": vector(7.78, -9.47) * mm});
            skLineSegment(sketch, "E196", {"start": v(56.13, 59.2) * mm, "end": v(58.5, 61.81) * mm});
            skLineSegment(sketch, "E197", {"start": v(58.5, 61.81) * mm, "end": v(60.87, 59.4) * mm});
            skLineSegment(sketch, "E198", {"start": v(60.87, 59.4) * mm, "end": v(61.13, 59.65) * mm});
            skLineSegment(sketch, "E199", {"start": v(61.13, 59.65) * mm, "end": v(58.67, 62.51) * mm});
            skLineSegment(sketch, "E200", {"start": v(58.67, 62.51) * mm, "end": v(62.25, 66.04) * mm});
            skLineSegment(sketch, "E201", {"start": v(62.25, 66.04) * mm, "end": v(65.73, 62.95) * mm});
            skLineSegment(sketch, "E202", {"start": v(65.73, 62.95) * mm, "end": v(65.97, 63.22) * mm});
            skLineSegment(sketch, "E203", {"start": v(65.97, 63.22) * mm, "end": v(63.07, 66.2) * mm});
            skLineSegment(sketch, "E204", {"start": v(63.07, 66.2) * mm, "end": v(65.28, 68.36) * mm});
            skLineSegment(sketch, "E205", {"start": v(65.28, 68.36) * mm, "end": v(68.9, 64.92) * mm});
            skLineSegment(sketch, "E206", {"start": v(68.9, 64.92) * mm, "end": v(69.4, 64.92) * mm});
            skLineSegment(sketch, "E207", {"start": v(69.4, 64.92) * mm, "end": v(65.59, 68.92) * mm});
            skLineSegment(sketch, "E208", {"start": v(65.59, 68.92) * mm, "end": v(65.18, 68.88) * mm});
            skLineSegment(sketch, "E209", {"start": v(63.95, 72) * mm, "end": v(64.23, 71.5) * mm});
            skLineSegment(sketch, "E210", {"start": v(64.94, 70.98) * mm, "end": v(65.28, 70.46) * mm});
            skLineSegment(sketch, "E211", {"start": v(65.9, 69.9) * mm, "end": v(71.77, 63.88) * mm});
            skFitSpline(sketch, "E212", {"points": [v(71.77, 63.88) * mm, v(70.96, 63.88) * mm, v(70.03, 63.62) * mm, v(68.52, 62.55) * mm, v(67.56, 61.98) * mm, v(66.57, 61.23) * mm, v(64.99, 59.2) * mm], "startDerivative": vector(-6.32, 0.23) * mm, "endDerivative": vector(-7.13, -10.05) * mm});
            skLineSegment(sketch, "E213.trimOffspring", {"start": v(56.13, 59.2) * mm, "end": v(52.99, 59.2) * mm});
            skLineSegment(sketch, "E214", {"start": v(93.82, 59.2) * mm, "end": v(94.16, 59.2) * mm});
            skSolve(sketch);
        }
        {
            var Q0;
            Q0 = qSketchRegion(id + "F0", true);
            extrude(context, id + "F2", {"entities" : qUnion([Q0]), "depth" : 10 * mm, "offsetDistance" : 25 * mm});
        }
        {
            var Q0;
            Q0 = qSketchRegion(id + "F1", true);
            var Q1;
            Q1=makeQuery(id+"F1.imprint","IMPRINT",FACE,{"disambiguationData":[TD([[makeQuery(id+"F1.imprint","IMPRINT",EDGE,{"derivedFrom":sQuery(id+"F1.wireOp",EDGE,"E107")}),1.0]])]});
            var Q2;
            Q2=makeQuery(id+"F1.imprint","IMPRINT",FACE,{"disambiguationData":[TD([[makeQuery(id+"F1.imprint","IMPRINT",EDGE,{"derivedFrom":sQuery(id+"F1.wireOp",EDGE,"E72")}),-1.0]])]});
            var Q3;
            Q3=makeQuery(id+"F1.imprint","IMPRINT",FACE,{"disambiguationData":[TD([[makeQuery(id+"F1.imprint","IMPRINT",EDGE,{"derivedFrom":sQuery(id+"F1.wireOp",EDGE,"E180")}),1.0]])]});
            var Q4;
            Q4=makeQuery(id+"F1.imprint","IMPRINT",FACE,{"disambiguationData":[TD([[makeQuery(id+"F1.imprint","IMPRINT",EDGE,{"derivedFrom":sQuery(id+"F1.wireOp",EDGE,"E167")}),-1.0]])]});
            var Q5;
            Q5=makeQuery(id+"F1.imprint","IMPRINT",FACE,{"disambiguationData":[TD([[makeQuery(id+"F1.imprint","IMPRINT",EDGE,{"derivedFrom":sQuery(id+"F1.wireOp",EDGE,"E164")}),-1.0]])]});
            var Q6;
            Q6=makeQuery(id+"F1.imprint","IMPRINT",FACE,{"disambiguationData":[TD([[makeQuery(id+"F1.imprint","IMPRINT",EDGE,{"derivedFrom":sQuery(id+"F1.wireOp",EDGE,"E113")}),1.0]])]});
            var Q7;
            Q7=makeQuery(id+"F1.imprint","IMPRINT",FACE,{"disambiguationData":[TD([[makeQuery(id+"F1.imprint","IMPRINT",EDGE,{"derivedFrom":sQuery(id+"F1.wireOp",EDGE,"E131")}),-1.0]])]});
            var Q8;
            Q8=makeQuery(id+"F1.imprint","IMPRINT",FACE,{"disambiguationData":[TD([[makeQuery(id+"F1.imprint","IMPRINT",EDGE,{"derivedFrom":sQuery(id+"F1.wireOp",EDGE,"E133")}),1.0]])]});
            var Q9;
            Q9=makeQuery(id+"F1.imprint","IMPRINT",FACE,{"disambiguationData":[TD([[makeQuery(id+"F1.imprint","IMPRINT",EDGE,{"derivedFrom":sQuery(id+"F1.wireOp",EDGE,"E137")}),1.0]])]});
            var Q10;
            Q10=makeQuery(id+"F1.imprint","IMPRINT",FACE,{"disambiguationData":[TD([[makeQuery(id+"F1.imprint","IMPRINT",EDGE,{"derivedFrom":sQuery(id+"F1.wireOp",EDGE,"E140")}),1.0]])]});
            var Q11;
            Q11=makeQuery(id+"F1.imprint","IMPRINT",FACE,{"disambiguationData":[TD([[makeQuery(id+"F1.imprint","IMPRINT",EDGE,{"derivedFrom":sQuery(id+"F1.wireOp",EDGE,"E71")}),1.0]])]});
            var Q12;
            Q12=makeQuery(id+"F1.imprint","IMPRINT",FACE,{"disambiguationData":[TD([[makeQuery(id+"F1.imprint","IMPRINT",EDGE,{"derivedFrom":sQuery(id+"F1.wireOp",EDGE,"E100")}),-1.0]])]});
            var Q13;
            Q13=makeQuery(id+"F1.imprint","IMPRINT",FACE,{"disambiguationData":[TD([[makeQuery(id+"F1.imprint","IMPRINT",EDGE,{"derivedFrom":sQuery(id+"F1.wireOp",EDGE,"E79")}),1.0]])]});
            var Q14;
            Q14=makeQuery(id+"F1.imprint","IMPRINT",FACE,{"disambiguationData":[TD([[makeQuery(id+"F1.imprint","IMPRINT",EDGE,{"derivedFrom":sQuery(id+"F1.wireOp",EDGE,"E114")}),1.0]])]});
            var Q15;
            Q15=makeQuery(id+"F1.imprint","IMPRINT",FACE,{"disambiguationData":[TD([[makeQuery(id+"F1.imprint","IMPRINT",EDGE,{"derivedFrom":sQuery(id+"F1.wireOp",EDGE,"E128")}),-1.0]])]});
            var Q16;
            Q16=makeQuery(id+"F1.imprint","IMPRINT",FACE,{"disambiguationData":[TD([[makeQuery(id+"F1.imprint","IMPRINT",EDGE,{"derivedFrom":sQuery(id+"F1.wireOp",EDGE,"E152")}),1.0]])]});
            var Q17;
            Q17=makeQuery(id+"F1.imprint","IMPRINT",FACE,{"disambiguationData":[TD([[makeQuery(id+"F1.imprint","IMPRINT",EDGE,{"derivedFrom":sQuery(id+"F1.wireOp",EDGE,"E146")}),1.0]])]});
            var Q18;
            Q18=makeQuery(id+"F1.imprint","IMPRINT",FACE,{"disambiguationData":[TD([[makeQuery(id+"F1.imprint","IMPRINT",EDGE,{"derivedFrom":sQuery(id+"F1.wireOp",EDGE,"E149")}),1.0]])]});
            extrude(context, id + "F3", {"entities" : qUnion([Q0, Q1, Q2, Q3, Q4, Q5, Q6, Q7, Q8, Q9, Q10, Q11, Q12, Q13, Q14, Q15, Q16, Q17, Q18]), "operationType" : NewBodyOperationType.ADD, "depth" : 13 * mm, "offsetDistance" : 25 * mm});
        }
        {
            var Q0;
            Q0=makeQuery(id+"F2.opExtrude","SWEPT_EDGE",EDGE,{"disambiguationData":[OSD([sQuery(id+"F0.wireOp",EDGE,"E1.0"),sQuery(id+"F0.wireOp",EDGE,"E1.1")])]});
            var Q1;
            Q1=makeQuery(id+"F2.opExtrude","SWEPT_EDGE",EDGE,{"disambiguationData":[OSD([sQuery(id+"F0.wireOp",EDGE,"E1.1"),sQuery(id+"F0.wireOp",EDGE,"E1.2")])]});
            var Q2;
            Q2=makeQuery(id+"F2.opExtrude","SWEPT_EDGE",EDGE,{"disambiguationData":[OSD([sQuery(id+"F0.wireOp",EDGE,"E1.3"),sQuery(id+"F0.wireOp",EDGE,"E2.trimOffspring")])]});
            var Q3;
            Q3=makeQuery(id+"F2.opExtrude","SWEPT_EDGE",EDGE,{"disambiguationData":[OSD([sQuery(id+"F0.wireOp",EDGE,"E1.3"),sQuery(id+"F0.wireOp",EDGE,"E4.trimOffspring")])]});
            var Q4;
            Q4=makeQuery(id+"F2.opExtrude","SWEPT_EDGE",EDGE,{"disambiguationData":[OSD([sQuery(id+"F0.wireOp",EDGE,"E2.trimOffspring"),sQuery(id+"F0.wireOp",EDGE,"E3.trimOffspring")])]});
            var Q5;
            Q5=makeQuery(id+"F2.opExtrude","SWEPT_EDGE",EDGE,{"disambiguationData":[OSD([sQuery(id+"F0.wireOp",EDGE,"E0"),sQuery(id+"F0.wireOp",EDGE,"E4.trimOffspring")])]});
            var Q6;
            Q6=makeQuery(id+"F2.opExtrude","SWEPT_EDGE",EDGE,{"disambiguationData":[OSD([sQuery(id+"F0.wireOp",EDGE,"E0"),sQuery(id+"F0.wireOp",EDGE,"E1.2")])]});
            var Q7;
            Q7=makeQuery(id+"F2.opExtrude","SWEPT_EDGE",EDGE,{"disambiguationData":[OSD([sQuery(id+"F0.wireOp",EDGE,"E1.0"),sQuery(id+"F0.wireOp",EDGE,"E3.trimOffspring")])]});
            fillet(context, id + "F4", {"entities" : qUnion([Q0, Q1, Q2, Q3, Q4, Q5, Q6, Q7]), "radius" : 3 * mm, "tangentPropagation" : true, "allowEdgeOverflow" : false});
        }
        {
            var Q0;
            Q0=qCreatedBy(makeId("Front.planeOp"),FACE);
            var sketch = newSketch(context, id + "F5", { "sketchPlane" : qUnion([Q0])});
            skCircle(sketch, "E215", {"center": v(0, 0) * mm, "radius": 18.36 * mm});
            skSolve(sketch);
        }
        {
            var Q0;
            Q0 = qSketchRegion(id + "F5", true);
            extrude(context, id + "F6", {"entities" : qUnion([Q0]), "depth" : 50 * mm, "offsetDistance" : 25 * mm});
        }
        {
            var Q0;
            Q0=makeQuery(id+"F6.opExtrude","CAP_FACE",FACE,{"disambiguationData":[OSD([sQuery(id+"F5.wireOp",EDGE,"E215")])],"isStart":false});
            var sketch = newSketch(context, id + "F7", { "sketchPlane" : qUnion([Q0])});
            skLineSegment(sketch, "E216.bottom", {"start": v(-8.06, -7.92) * mm, "end": v(8.53, -7.92) * mm});
            skLineSegment(sketch, "E216.top", {"start": v(-8.06, 8.62) * mm, "end": v(8.53, 8.62) * mm});
            skLineSegment(sketch, "E216.left", {"start": v(-8.06, -7.92) * mm, "end": v(-8.06, 8.62) * mm});
            skLineSegment(sketch, "E216.right", {"start": v(8.53, -7.92) * mm, "end": v(8.53, 8.62) * mm});
            skSolve(sketch);
        }
        {
            var Q0;
            Q0=makeQuery(id+"F7.imprint","IMPRINT",FACE,{"disambiguationData":[TD([[makeQuery(id+"F7.imprint","IMPRINT",EDGE,{"derivedFrom":sQuery(id+"F7.wireOp",EDGE,"E216.bottom")}),1.0]])]});
            extrude(context, id + "F8", {"entities" : qUnion([Q0]), "operationType" : NewBodyOperationType.REMOVE, "oppositeDirection" : true, "depth" : 100 * mm, "offsetDistance" : 25 * mm});
        }
    });
